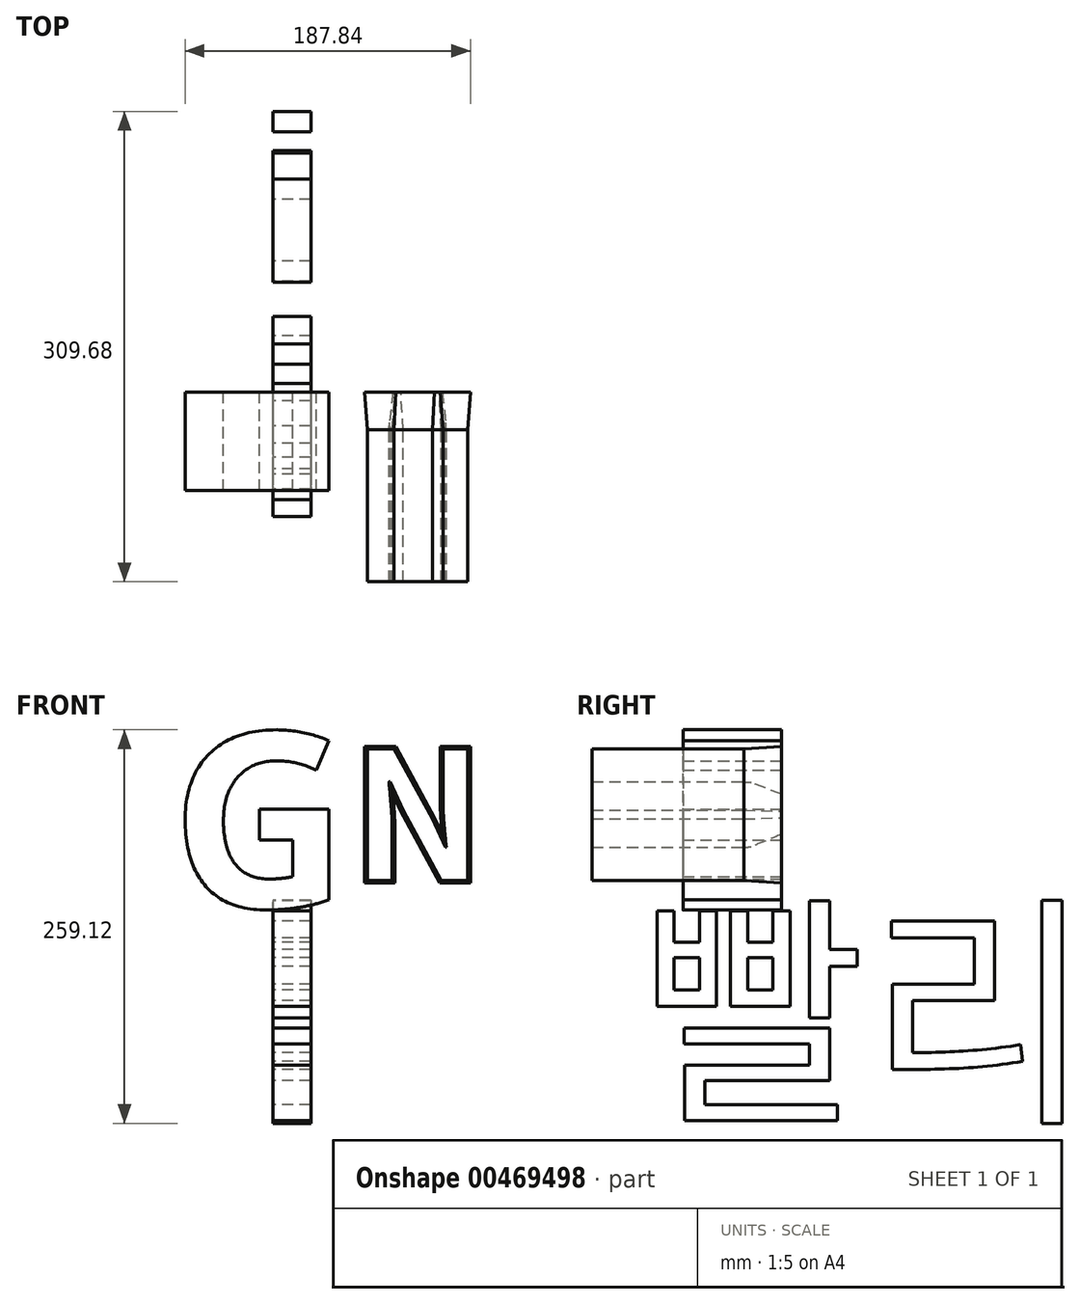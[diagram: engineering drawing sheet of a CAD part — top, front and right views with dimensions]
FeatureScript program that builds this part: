
annotation { "Feature Type Name" : "Feature", "Feature Type Description" : "" }
export const myFeature = defineFeature(function(context is Context, id is Id, definition is map)
    precondition{}
    {
        {
            var Q0;
            Q0=qCreatedBy(makeId("Front.planeOp"),FACE);
            var sketch = newSketch(context, id + "F0", { "sketchPlane" : qUnion([Q0])});
            skText(sketch, "E0", { "text": "GNGNNG", "fontName": "OpenSans-Bold.ttf"});
            const initialGuessF0  = {"E0": [-0.06712, -0.04817, 1, 0, 0.11637]};
            skSetInitialGuess(sketch, initialGuessF0);
            skSolve(sketch);
        }
        {
            var Q0;
            Q0=makeQuery(id+"F0.imprint","IMPRINT",FACE,{"disambiguationData":[TD([[makeQuery(id+"F0.imprint","IMPRINT",EDGE,{"derivedFrom":sQuery(id+"F0.wireOp",EDGE,"E0.sketch_text.stroke-0")}),-1.0]])]});
            extrude(context, id + "F1", {"entities" : qUnion([Q0]), "depth" : 40 * mm, "hasSecondDirection" : true, "secondDirectionOppositeDirection" : true, "secondDirectionDepth" : 25 * mm});
        }
        {
            var Q0;
            Q0=qCreatedBy(makeId("Front.planeOp"),FACE);
            var sketch = newSketch(context, id + "F2", { "sketchPlane" : qUnion([Q0])});
            skText(sketch, "E1", { "text": "N", "fontName": "NotoSansCJKkr-Bold.otf"});
            const initialGuessF2  = {"E1": [0.05164, -0.03023, 1, 0, 0.08407]};
            skSetInitialGuess(sketch, initialGuessF2);
            skSolve(sketch);
        }
        {
            var Q0;
            Q0 = qSketchRegion(id + "F2", true);
            extrude(context, id + "F3", {"entities" : qUnion([Q0]), "depth" : 100 * mm, "hasSecondDirection" : true, "secondDirectionOppositeDirection" : true, "secondDirectionDepth" : 25 * mm, "hasSecondDirectionDraft" : true, "secondDirectionDraftAngle" : 4 * degree});
        }
        {
            var Q0;
            Q0=qCreatedBy(makeId("Right.planeOp"),FACE);
            var sketch = newSketch(context, id + "F4", { "sketchPlane" : qUnion([Q0])});
            skText(sketch, "E2", { "text": "빨리", "fontName": "NotoSansCJKkr-Regular.otf"});
            const initialGuessF4  = {"E2": [-0.06966, -0.178, 1, 0, 0.11768]};
            skSetInitialGuess(sketch, initialGuessF4);
            skSolve(sketch);
        }
        {
            var Q0;
            Q0=makeQuery(id+"F4.imprint","IMPRINT",FACE,{"disambiguationData":[TD([[makeQuery(id+"F4.imprint","IMPRINT",EDGE,{"derivedFrom":sQuery(id+"F4.wireOp",EDGE,"E2.sketch_text.stroke-57")}),1.0]])]});
            var Q1;
            Q1=makeQuery(id+"F4.imprint","IMPRINT",FACE,{"disambiguationData":[TD([[makeQuery(id+"F4.imprint","IMPRINT",EDGE,{"derivedFrom":sQuery(id+"F4.wireOp",EDGE,"E2.sketch_text.stroke-44")}),1.0]])]});
            var Q2;
            Q2=makeQuery(id+"F4.imprint","IMPRINT",FACE,{"disambiguationData":[TD([[makeQuery(id+"F4.imprint","IMPRINT",EDGE,{"derivedFrom":sQuery(id+"F4.wireOp",EDGE,"E2.sketch_text.stroke-24")}),1.0]])]});
            var Q3;
            Q3=makeQuery(id+"F4.imprint","IMPRINT",FACE,{"disambiguationData":[TD([[makeQuery(id+"F4.imprint","IMPRINT",EDGE,{"derivedFrom":sQuery(id+"F4.wireOp",EDGE,"E2.sketch_text.stroke-36")}),1.0]])]});
            var Q4;
            Q4=makeQuery(id+"F4.imprint","IMPRINT",FACE,{"disambiguationData":[TD([[makeQuery(id+"F4.imprint","IMPRINT",EDGE,{"derivedFrom":sQuery(id+"F4.wireOp",EDGE,"E2.sketch_text.stroke-0")}),1.0]])]});
            var Q5;
            Q5=makeQuery(id+"F4.imprint","IMPRINT",FACE,{"disambiguationData":[TD([[makeQuery(id+"F4.imprint","IMPRINT",EDGE,{"derivedFrom":sQuery(id+"F4.wireOp",EDGE,"E2.sketch_text.stroke-12")}),1.0]])]});
            extrude(context, id + "F5", {"entities" : qUnion([Q0, Q1, Q2, Q3, Q4, Q5]), "depth" : 25 * mm});
        }
    });
